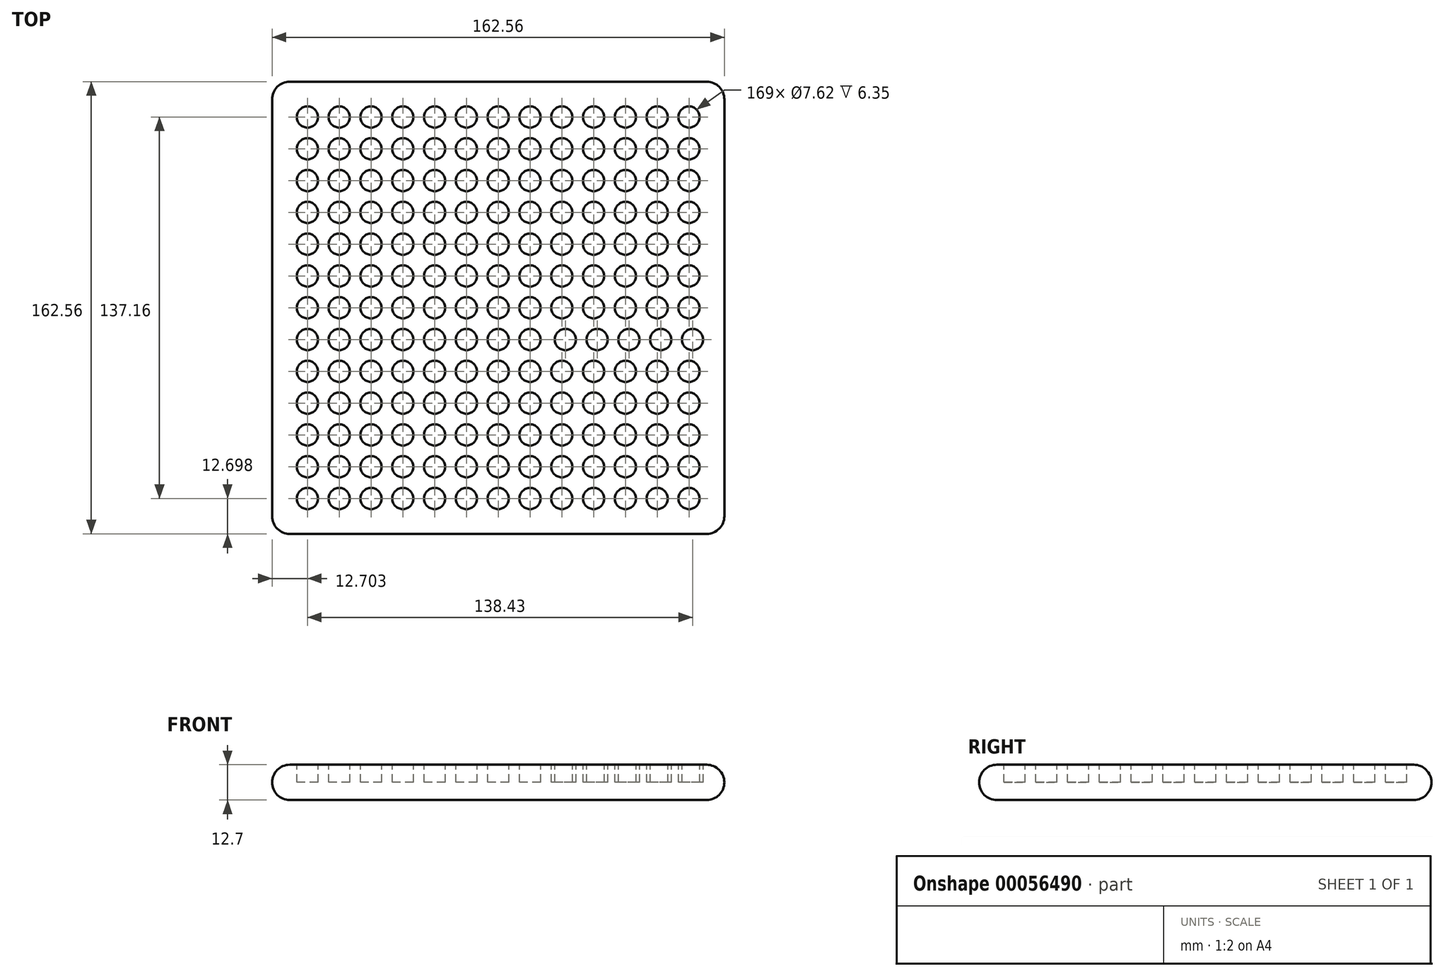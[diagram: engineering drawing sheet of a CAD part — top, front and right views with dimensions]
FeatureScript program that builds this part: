
annotation { "Feature Type Name" : "Feature", "Feature Type Description" : "" }
export const myFeature = defineFeature(function(context is Context, id is Id, definition is map)
    precondition{}
    {
        {
            var Q0;
            Q0=qCreatedBy(makeId("Top.planeOp"),FACE);
            var sketch = newSketch(context, id + "F0", { "sketchPlane" : qUnion([Q0])});
            skLineSegment(sketch, "E0.bottom", {"start": v(-144.62, 173.78) * mm, "end": v(17.94, 173.78) * mm});
            skLineSegment(sketch, "E0.top", {"start": v(-144.62, 11.22) * mm, "end": v(17.94, 11.22) * mm});
            skLineSegment(sketch, "E0.left", {"start": v(-144.62, 173.78) * mm, "end": v(-144.62, 11.22) * mm});
            skLineSegment(sketch, "E0.right", {"start": v(17.94, 173.78) * mm, "end": v(17.94, 11.22) * mm});
            skSolve(sketch);
        }
        {
            var Q0;
            Q0=qSketchRegion(id+"F0",true);
            extrude(context, id + "F1", {"entities" : qUnion([Q0]), "depth" : 12.7 * mm});
        }
        {
            var Q0;
            Q0=makeQuery(id+"F1.opExtrude","CAP_FACE",FACE,{"disambiguationData":[OSD([sQuery(id+"F0.wireOp",EDGE,"E0.bottom"),sQuery(id+"F0.wireOp",EDGE,"E0.top"),sQuery(id+"F0.wireOp",EDGE,"E0.left"),sQuery(id+"F0.wireOp",EDGE,"E0.right")])],"isStart":false});
            var sketch = newSketch(context, id + "F2", { "sketchPlane" : qUnion([Q0])});
            skSolve(sketch);
        }
        {
            var Q0;
            Q0=makeQuery(id+"F2.imprint","IMPRINT",FACE,{"disambiguationData":[TD([[makeQuery(id+"F2.imprint","IMPRINT",EDGE,{"derivedFrom":makeQuery(id+"F1.opExtrude","CAP_EDGE",EDGE,{"disambiguationData":[OSD([sQuery(id+"F0.wireOp",EDGE,"E0.bottom")])],"isStart":false})}),-1.0]])]});
            var sketch = newSketch(context, id + "F3", { "sketchPlane" : qUnion([Q0])});
            skCircle(sketch, "E1", {"center": v(-131.92, 23.92) * mm, "radius": 3.81 * mm});
            skCircle(sketch, "E2", {"center": v(-86.2, 23.92) * mm, "radius": 3.81 * mm});
            skCircle(sketch, "E3", {"center": v(-40.48, 23.92) * mm, "radius": 3.81 * mm});
            skCircle(sketch, "E4", {"center": v(5.24, 23.92) * mm, "radius": 3.81 * mm});
            skCircle(sketch, "E5", {"center": v(-109.06, 23.92) * mm, "radius": 3.81 * mm});
            skCircle(sketch, "E6", {"center": v(-63.34, 23.92) * mm, "radius": 3.81 * mm});
            skCircle(sketch, "E7", {"center": v(-17.62, 23.92) * mm, "radius": 3.81 * mm});
            skCircle(sketch, "E8", {"center": v(-131.92, 46.78) * mm, "radius": 3.81 * mm});
            skCircle(sketch, "E9", {"center": v(-131.92, 69.64) * mm, "radius": 3.81 * mm});
            skCircle(sketch, "E10", {"center": v(-131.92, 92.5) * mm, "radius": 3.81 * mm});
            skCircle(sketch, "E11", {"center": v(-131.92, 115.36) * mm, "radius": 3.81 * mm});
            skCircle(sketch, "E12", {"center": v(-131.92, 138.22) * mm, "radius": 3.81 * mm});
            skCircle(sketch, "E13", {"center": v(-131.92, 161.08) * mm, "radius": 3.81 * mm});
            skCircle(sketch, "E14", {"center": v(-109.06, 46.78) * mm, "radius": 3.81 * mm});
            skCircle(sketch, "E15", {"center": v(-109.06, 69.64) * mm, "radius": 3.81 * mm});
            skCircle(sketch, "E16", {"center": v(-109.06, 92.5) * mm, "radius": 3.81 * mm});
            skCircle(sketch, "E17", {"center": v(-109.06, 115.36) * mm, "radius": 3.81 * mm});
            skCircle(sketch, "E18", {"center": v(-109.06, 138.22) * mm, "radius": 3.81 * mm});
            skCircle(sketch, "E19", {"center": v(-109.06, 161.08) * mm, "radius": 3.81 * mm});
            skCircle(sketch, "E20", {"center": v(-86.2, 46.78) * mm, "radius": 3.81 * mm});
            skCircle(sketch, "E21", {"center": v(-63.34, 46.78) * mm, "radius": 3.81 * mm});
            skCircle(sketch, "E22", {"center": v(-40.48, 46.78) * mm, "radius": 3.81 * mm});
            skCircle(sketch, "E23", {"center": v(188.12, 46.78) * mm, "radius": 3.81 * mm});
            skCircle(sketch, "E24", {"center": v(5.24, 46.78) * mm, "radius": 3.81 * mm});
            skCircle(sketch, "E25", {"center": v(-17.62, 46.78) * mm, "radius": 3.81 * mm});
            skCircle(sketch, "E26", {"center": v(-86.2, 161.08) * mm, "radius": 3.81 * mm});
            skCircle(sketch, "E27", {"center": v(-86.2, 138.22) * mm, "radius": 3.81 * mm});
            skCircle(sketch, "E28", {"center": v(-86.2, 115.36) * mm, "radius": 3.81 * mm});
            skCircle(sketch, "E29", {"center": v(-86.2, 92.5) * mm, "radius": 3.81 * mm});
            skCircle(sketch, "E30", {"center": v(-86.2, 69.64) * mm, "radius": 3.81 * mm});
            skCircle(sketch, "E31", {"center": v(-63.34, 69.64) * mm, "radius": 3.81 * mm});
            skCircle(sketch, "E32", {"center": v(-40.48, 69.64) * mm, "radius": 3.81 * mm});
            skCircle(sketch, "E33", {"center": v(-17.62, 69.64) * mm, "radius": 3.81 * mm});
            skCircle(sketch, "E34", {"center": v(5.24, 69.64) * mm, "radius": 3.81 * mm});
            skCircle(sketch, "E35", {"center": v(-63.34, 92.5) * mm, "radius": 3.81 * mm});
            skCircle(sketch, "E36", {"center": v(-40.48, 92.5) * mm, "radius": 3.81 * mm});
            skCircle(sketch, "E37", {"center": v(-17.62, 92.5) * mm, "radius": 3.81 * mm});
            skCircle(sketch, "E38", {"center": v(5.24, 92.5) * mm, "radius": 3.81 * mm});
            skCircle(sketch, "E39", {"center": v(-17.62, 161.08) * mm, "radius": 3.81 * mm});
            skCircle(sketch, "E40", {"center": v(-63.34, 115.36) * mm, "radius": 3.81 * mm});
            skCircle(sketch, "E41", {"center": v(-63.34, 161.08) * mm, "radius": 3.81 * mm});
            skCircle(sketch, "E42", {"center": v(-17.62, 138.22) * mm, "radius": 3.81 * mm});
            skCircle(sketch, "E43", {"center": v(-40.48, 138.22) * mm, "radius": 3.81 * mm});
            skCircle(sketch, "E44", {"center": v(-40.48, 161.08) * mm, "radius": 3.81 * mm});
            skCircle(sketch, "E45", {"center": v(5.24, 115.36) * mm, "radius": 3.81 * mm});
            skCircle(sketch, "E46", {"center": v(5.24, 138.22) * mm, "radius": 3.81 * mm});
            skCircle(sketch, "E47", {"center": v(-40.48, 115.36) * mm, "radius": 3.81 * mm});
            skCircle(sketch, "E48", {"center": v(-63.34, 138.22) * mm, "radius": 3.81 * mm});
            skCircle(sketch, "E49", {"center": v(5.24, 161.08) * mm, "radius": 3.81 * mm});
            skCircle(sketch, "E50", {"center": v(-17.62, 115.36) * mm, "radius": 3.81 * mm});
            skCircle(sketch, "E51", {"center": v(-120.49, 161.08) * mm, "radius": 3.81 * mm});
            skCircle(sketch, "E52", {"center": v(-131.92, 149.65) * mm, "radius": 3.81 * mm});
            skCircle(sketch, "E53", {"center": v(-120.49, 149.65) * mm, "radius": 3.81 * mm});
            skCircle(sketch, "E54", {"center": v(-109.06, 149.65) * mm, "radius": 3.81 * mm});
            skCircle(sketch, "E55", {"center": v(-120.49, 138.22) * mm, "radius": 3.81 * mm});
            skCircle(sketch, "E56", {"center": v(-97.63, 161.08) * mm, "radius": 3.81 * mm});
            skCircle(sketch, "E57", {"center": v(-97.63, 149.65) * mm, "radius": 3.81 * mm});
            skCircle(sketch, "E58", {"center": v(-97.63, 138.22) * mm, "radius": 3.81 * mm});
            skCircle(sketch, "E59", {"center": v(-86.2, 149.65) * mm, "radius": 3.81 * mm});
            skCircle(sketch, "E60", {"center": v(-74.77, 161.08) * mm, "radius": 3.81 * mm});
            skCircle(sketch, "E61", {"center": v(-74.77, 149.65) * mm, "radius": 3.81 * mm});
            skCircle(sketch, "E62", {"center": v(-74.77, 138.22) * mm, "radius": 3.81 * mm});
            skCircle(sketch, "E63", {"center": v(-63.34, 149.65) * mm, "radius": 3.81 * mm});
            skCircle(sketch, "E64", {"center": v(-51.9, 161.08) * mm, "radius": 3.81 * mm});
            skCircle(sketch, "E65", {"center": v(-51.9, 149.65) * mm, "radius": 3.81 * mm});
            skCircle(sketch, "E66", {"center": v(-51.9, 138.22) * mm, "radius": 3.81 * mm});
            skCircle(sketch, "E67", {"center": v(-40.48, 149.65) * mm, "radius": 3.81 * mm});
            skCircle(sketch, "E68", {"center": v(-29.05, 161.08) * mm, "radius": 3.81 * mm});
            skCircle(sketch, "E69", {"center": v(-29.05, 149.65) * mm, "radius": 3.81 * mm});
            skCircle(sketch, "E70", {"center": v(-29.05, 138.22) * mm, "radius": 3.81 * mm});
            skCircle(sketch, "E71", {"center": v(-17.62, 149.65) * mm, "radius": 3.81 * mm});
            skCircle(sketch, "E72", {"center": v(-6.19, 161.08) * mm, "radius": 3.81 * mm});
            skCircle(sketch, "E73", {"center": v(-6.19, 149.65) * mm, "radius": 3.81 * mm});
            skCircle(sketch, "E74", {"center": v(5.24, 149.65) * mm, "radius": 3.81 * mm});
            skCircle(sketch, "E75", {"center": v(-6.19, 138.22) * mm, "radius": 3.81 * mm});
            skCircle(sketch, "E76", {"center": v(-131.92, 126.79) * mm, "radius": 3.81 * mm});
            skCircle(sketch, "E77", {"center": v(-131.92, 103.93) * mm, "radius": 3.81 * mm});
            skCircle(sketch, "E78", {"center": v(-120.49, 126.79) * mm, "radius": 3.81 * mm});
            skCircle(sketch, "E79", {"center": v(-109.06, 126.79) * mm, "radius": 3.81 * mm});
            skCircle(sketch, "E80", {"center": v(-120.49, 115.36) * mm, "radius": 3.81 * mm});
            skCircle(sketch, "E81", {"center": v(-120.49, 103.93) * mm, "radius": 3.81 * mm});
            skCircle(sketch, "E82", {"center": v(-109.06, 103.93) * mm, "radius": 3.81 * mm});
            skCircle(sketch, "E83", {"center": v(-120.49, 92.5) * mm, "radius": 3.81 * mm});
            skCircle(sketch, "E84", {"center": v(-120.49, 81.07) * mm, "radius": 3.81 * mm});
            skCircle(sketch, "E85", {"center": v(-109.06, 81.07) * mm, "radius": 3.81 * mm});
            skCircle(sketch, "E86", {"center": v(-131.92, 81.07) * mm, "radius": 3.81 * mm});
            skCircle(sketch, "E87", {"center": v(-120.49, 69.64) * mm, "radius": 3.81 * mm});
            skCircle(sketch, "E88", {"center": v(-109.06, 58.2) * mm, "radius": 3.81 * mm});
            skCircle(sketch, "E89", {"center": v(-120.49, 58.2) * mm, "radius": 3.81 * mm});
            skCircle(sketch, "E90", {"center": v(-131.92, 58.2) * mm, "radius": 3.81 * mm});
            skCircle(sketch, "E91", {"center": v(-120.49, 46.78) * mm, "radius": 3.81 * mm});
            skCircle(sketch, "E92", {"center": v(-120.49, 23.92) * mm, "radius": 3.81 * mm});
            skCircle(sketch, "E93", {"center": v(-120.49, 35.35) * mm, "radius": 3.81 * mm});
            skCircle(sketch, "E94", {"center": v(-109.06, 35.35) * mm, "radius": 3.81 * mm});
            skCircle(sketch, "E95", {"center": v(-131.92, 35.35) * mm, "radius": 3.81 * mm});
            skCircle(sketch, "E96", {"center": v(-97.63, 126.79) * mm, "radius": 3.81 * mm});
            skCircle(sketch, "E97", {"center": v(-86.2, 126.79) * mm, "radius": 3.81 * mm});
            skCircle(sketch, "E98", {"center": v(-97.63, 115.36) * mm, "radius": 3.81 * mm});
            skCircle(sketch, "E99", {"center": v(-74.77, 115.36) * mm, "radius": 3.81 * mm});
            skCircle(sketch, "E100", {"center": v(-74.77, 126.79) * mm, "radius": 3.81 * mm});
            skCircle(sketch, "E101", {"center": v(-63.34, 126.79) * mm, "radius": 3.81 * mm});
            skCircle(sketch, "E102", {"center": v(-51.9, 126.79) * mm, "radius": 3.81 * mm});
            skCircle(sketch, "E103", {"center": v(-51.9, 115.36) * mm, "radius": 3.81 * mm});
            skCircle(sketch, "E104", {"center": v(-40.48, 126.79) * mm, "radius": 3.81 * mm});
            skCircle(sketch, "E105", {"center": v(-29.05, 126.79) * mm, "radius": 3.81 * mm});
            skCircle(sketch, "E106", {"center": v(-17.62, 126.79) * mm, "radius": 3.81 * mm});
            skCircle(sketch, "E107", {"center": v(-29.05, 115.36) * mm, "radius": 3.81 * mm});
            skCircle(sketch, "E108", {"center": v(-6.19, 126.79) * mm, "radius": 3.81 * mm});
            skCircle(sketch, "E109", {"center": v(5.24, 126.79) * mm, "radius": 3.81 * mm});
            skCircle(sketch, "E110", {"center": v(-6.19, 115.36) * mm, "radius": 3.81 * mm});
            skCircle(sketch, "E111", {"center": v(-97.63, 103.93) * mm, "radius": 3.81 * mm});
            skCircle(sketch, "E112", {"center": v(-97.63, 92.5) * mm, "radius": 3.81 * mm});
            skCircle(sketch, "E113", {"center": v(-86.2, 103.93) * mm, "radius": 3.81 * mm});
            skCircle(sketch, "E114", {"center": v(-74.77, 103.93) * mm, "radius": 3.81 * mm});
            skCircle(sketch, "E115", {"center": v(-74.77, 92.5) * mm, "radius": 3.81 * mm});
            skCircle(sketch, "E116", {"center": v(-63.34, 103.93) * mm, "radius": 3.81 * mm});
            skCircle(sketch, "E117", {"center": v(-51.9, 103.93) * mm, "radius": 3.81 * mm});
            skCircle(sketch, "E118", {"center": v(-51.9, 92.5) * mm, "radius": 3.81 * mm});
            skCircle(sketch, "E119", {"center": v(-40.48, 103.93) * mm, "radius": 3.81 * mm});
            skCircle(sketch, "E120", {"center": v(-29.05, 103.93) * mm, "radius": 3.81 * mm});
            skCircle(sketch, "E121", {"center": v(-29.05, 92.5) * mm, "radius": 3.81 * mm});
            skCircle(sketch, "E122", {"center": v(-17.62, 103.93) * mm, "radius": 3.81 * mm});
            skCircle(sketch, "E123", {"center": v(-6.19, 103.93) * mm, "radius": 3.81 * mm});
            skCircle(sketch, "E124", {"center": v(5.24, 103.93) * mm, "radius": 3.81 * mm});
            skCircle(sketch, "E125", {"center": v(-6.19, 92.5) * mm, "radius": 3.81 * mm});
            skCircle(sketch, "E126", {"center": v(-39.2, 81.07) * mm, "radius": 3.81 * mm});
            skCircle(sketch, "E127", {"center": v(-27.78, 81.07) * mm, "radius": 3.81 * mm});
            skCircle(sketch, "E128", {"center": v(-29.05, 69.64) * mm, "radius": 3.81 * mm});
            skCircle(sketch, "E129", {"center": v(-16.35, 81.07) * mm, "radius": 3.81 * mm});
            skCircle(sketch, "E130", {"center": v(-4.92, 81.07) * mm, "radius": 3.81 * mm});
            skCircle(sketch, "E131", {"center": v(6.51, 81.07) * mm, "radius": 3.81 * mm});
            skCircle(sketch, "E132", {"center": v(-6.19, 69.64) * mm, "radius": 3.81 * mm});
            skCircle(sketch, "E133", {"center": v(5.24, 58.2) * mm, "radius": 3.81 * mm});
            skCircle(sketch, "E134", {"center": v(-6.19, 58.2) * mm, "radius": 3.81 * mm});
            skCircle(sketch, "E135", {"center": v(-29.05, 58.2) * mm, "radius": 3.81 * mm});
            skCircle(sketch, "E136", {"center": v(-17.62, 58.2) * mm, "radius": 3.81 * mm});
            skCircle(sketch, "E137", {"center": v(-29.05, 46.78) * mm, "radius": 3.81 * mm});
            skCircle(sketch, "E138", {"center": v(-6.19, 46.78) * mm, "radius": 3.81 * mm});
            skCircle(sketch, "E139", {"center": v(-29.05, 35.35) * mm, "radius": 3.81 * mm});
            skCircle(sketch, "E140", {"center": v(-40.48, 35.35) * mm, "radius": 3.81 * mm});
            skCircle(sketch, "E141", {"center": v(-17.62, 35.35) * mm, "radius": 3.81 * mm});
            skCircle(sketch, "E142", {"center": v(-6.19, 35.35) * mm, "radius": 3.81 * mm});
            skCircle(sketch, "E143", {"center": v(5.24, 35.35) * mm, "radius": 3.81 * mm});
            skCircle(sketch, "E144", {"center": v(-29.05, 23.92) * mm, "radius": 3.81 * mm});
            skCircle(sketch, "E145", {"center": v(-6.19, 23.92) * mm, "radius": 3.81 * mm});
            skCircle(sketch, "E146", {"center": v(-40.48, 58.2) * mm, "radius": 3.81 * mm});
            skCircle(sketch, "E147", {"center": v(-86.2, 81.07) * mm, "radius": 3.81 * mm});
            skCircle(sketch, "E148", {"center": v(-74.77, 81.07) * mm, "radius": 3.81 * mm});
            skCircle(sketch, "E149", {"center": v(-63.34, 81.07) * mm, "radius": 3.81 * mm});
            skCircle(sketch, "E150", {"center": v(-97.63, 81.07) * mm, "radius": 3.81 * mm});
            skCircle(sketch, "E151", {"center": v(-97.63, 69.64) * mm, "radius": 3.81 * mm});
            skCircle(sketch, "E152", {"center": v(-74.77, 69.64) * mm, "radius": 3.81 * mm});
            skCircle(sketch, "E153", {"center": v(-51.9, 69.64) * mm, "radius": 3.81 * mm});
            skCircle(sketch, "E154", {"center": v(-51.9, 81.07) * mm, "radius": 3.81 * mm});
            skCircle(sketch, "E155", {"center": v(-97.63, 58.2) * mm, "radius": 3.81 * mm});
            skCircle(sketch, "E156", {"center": v(-86.2, 58.2) * mm, "radius": 3.81 * mm});
            skCircle(sketch, "E157", {"center": v(-74.77, 58.2) * mm, "radius": 3.81 * mm});
            skCircle(sketch, "E158", {"center": v(-63.34, 58.2) * mm, "radius": 3.81 * mm});
            skCircle(sketch, "E159", {"center": v(-51.9, 58.2) * mm, "radius": 3.81 * mm});
            skCircle(sketch, "E160", {"center": v(-51.9, 46.78) * mm, "radius": 3.81 * mm});
            skCircle(sketch, "E161", {"center": v(-51.9, 35.35) * mm, "radius": 3.81 * mm});
            skCircle(sketch, "E162", {"center": v(-51.9, 23.92) * mm, "radius": 3.81 * mm});
            skCircle(sketch, "E163", {"center": v(-63.34, 35.35) * mm, "radius": 3.81 * mm});
            skCircle(sketch, "E164", {"center": v(-74.77, 46.78) * mm, "radius": 3.81 * mm});
            skCircle(sketch, "E165", {"center": v(-74.77, 35.35) * mm, "radius": 3.81 * mm});
            skCircle(sketch, "E166", {"center": v(-74.77, 23.92) * mm, "radius": 3.81 * mm});
            skCircle(sketch, "E167", {"center": v(-86.2, 35.35) * mm, "radius": 3.81 * mm});
            skCircle(sketch, "E168", {"center": v(-97.63, 46.78) * mm, "radius": 3.81 * mm});
            skCircle(sketch, "E169", {"center": v(-97.63, 35.35) * mm, "radius": 3.81 * mm});
            skCircle(sketch, "E170", {"center": v(-97.63, 23.92) * mm, "radius": 3.81 * mm});
            skSolve(sketch);
        }
        {
            var Q0;
            Q0=qSketchRegion(id+"F3",true);
            extrude(context, id + "F4", {"entities" : qUnion([Q0]), "operationType" : NewBodyOperationType.REMOVE, "oppositeDirection" : true, "depth" : 6.35 * mm});
        }
        {
            var Q0;
            Q0=makeQuery(id+"F1.opExtrude","SWEPT_FACE",FACE,{"disambiguationData":[OSD([sQuery(id+"F0.wireOp",EDGE,"E0.top")])]});
            var Q1;
            Q1=makeQuery(id+"F1.opExtrude","SWEPT_FACE",FACE,{"disambiguationData":[OSD([sQuery(id+"F0.wireOp",EDGE,"E0.left")])]});
            var Q2;
            Q2=makeQuery(id+"F1.opExtrude","SWEPT_FACE",FACE,{"disambiguationData":[OSD([sQuery(id+"F0.wireOp",EDGE,"E0.bottom")])]});
            var Q3;
            Q3=makeQuery(id+"F1.opExtrude","SWEPT_FACE",FACE,{"disambiguationData":[OSD([sQuery(id+"F0.wireOp",EDGE,"E0.right")])]});
            fillet(context, id + "F5", {"entities" : qUnion([Q0, Q1, Q2, Q3]), "radius" : 6.35 * mm, "tangentPropagation" : true, "allowEdgeOverflow" : false});
        }
    });
